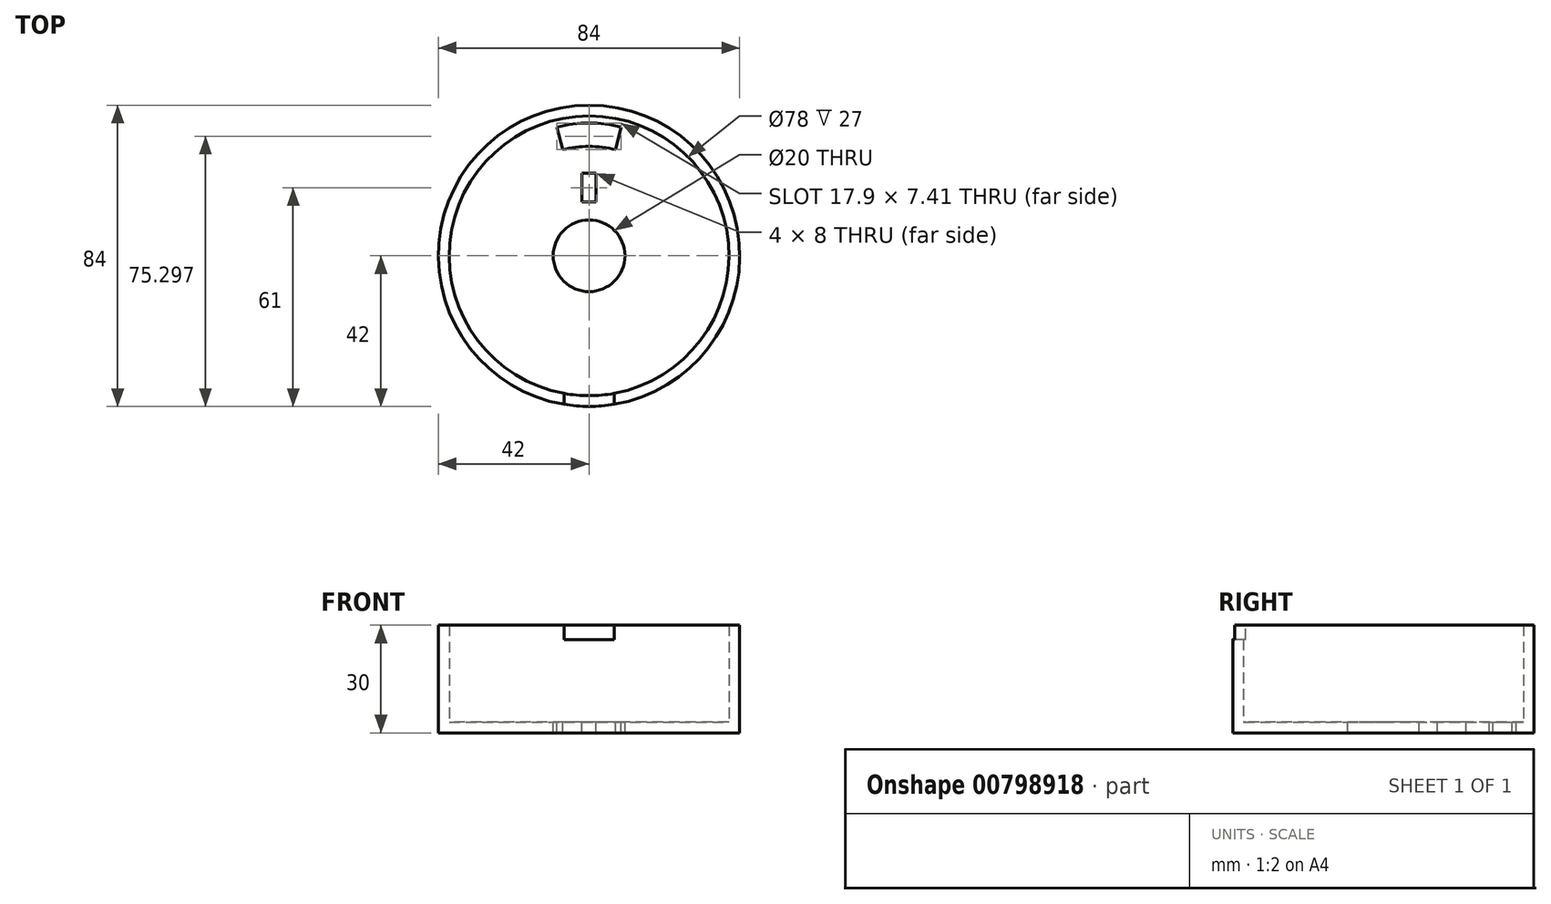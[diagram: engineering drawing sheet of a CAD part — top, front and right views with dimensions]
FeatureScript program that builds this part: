
annotation { "Feature Type Name" : "Feature", "Feature Type Description" : "" }
export const myFeature = defineFeature(function(context is Context, id is Id, definition is map)
    precondition{}
    {
        {
            var Q0;
            Q0=qCreatedBy(makeId("Top.planeOp"),FACE);
            var sketch = newSketch(context, id + "F0", { "sketchPlane" : qUnion([Q0])});
            skCircle(sketch, "E0", {"center": v(0, 0) * mm, "radius": 42 * mm});
            skSolve(sketch);
        }
        {
            var Q0;
            Q0=makeQuery(id+"F0.imprint","IMPRINT",FACE,{"disambiguationData":[TD([[makeQuery(id+"F0.imprint","IMPRINT",EDGE,{"derivedFrom":sQuery(id+"F0.wireOp",EDGE,"E0")}),1.0]])]});
            extrude(context, id + "F1", {"entities" : qUnion([Q0]), "depth" : 3 * mm, "offsetDistance" : 25.4 * mm});
        }
        {
            var Q0;
            Q0=makeQuery(id+"F1.opExtrude","CAP_FACE",FACE,{"disambiguationData":[OSD([sQuery(id+"F0.wireOp",EDGE,"E0")])],"isStart":false});
            var sketch = newSketch(context, id + "F2", { "sketchPlane" : qUnion([Q0])});
            skCircle(sketch, "E1", {"center": v(0, 0) * mm, "radius": 39 * mm});
            skCircle(sketch, "E2", {"center": v(0, 0) * mm, "radius": 42 * mm});
            skSolve(sketch);
        }
        {
            var Q0;
            Q0=makeQuery(id+"F2.imprint","IMPRINT",FACE,{"disambiguationData":[TD([[makeQuery(id+"F2.imprint","IMPRINT",EDGE,{"derivedFrom":sQuery(id+"F2.wireOp",EDGE,"E1")}),-1.0]])]});
            extrude(context, id + "F3", {"entities" : qUnion([Q0]), "operationType" : NewBodyOperationType.ADD, "depth" : 27 * mm, "offsetDistance" : 25.4 * mm});
        }
        {
            var Q0;
            Q0=makeQuery(id+"F3.opExtrude","CAP_FACE",FACE,{"disambiguationData":[OSD([sQuery(id+"F2.wireOp",EDGE,"E1"),sQuery(id+"F2.wireOp",EDGE,"E2")])],"isStart":false});
            var sketch = newSketch(context, id + "F4", { "sketchPlane" : qUnion([Q0])});
            skLineSegment(sketch, "E3.bottom", {"start": v(-7, -34.99) * mm, "end": v(7, -34.99) * mm});
            skLineSegment(sketch, "E3.top", {"start": v(-7, -46.24) * mm, "end": v(7, -46.24) * mm});
            skLineSegment(sketch, "E3.left", {"start": v(-7, -34.99) * mm, "end": v(-7, -46.24) * mm});
            skLineSegment(sketch, "E3.right", {"start": v(7, -34.99) * mm, "end": v(7, -46.24) * mm});
            skSolve(sketch);
        }
        {
            var Q0;
            {var subQ0=sQuery(id+"F4.wireOp",EDGE,"E3.left");var subQ1=makeQuery(id+"F3.opExtrude","CAP_EDGE",EDGE,{"disambiguationData":[OSD([sQuery(id+"F2.wireOp",EDGE,"E2")])],"isStart":false});var subQ2=makeQuery(id+"F4.imprint","INTERSECT",VERTEX,{"derivedFrom":[subQ1,subQ0]});Q0=makeQuery(id+"F4.imprint","IMPRINT",FACE,{"disambiguationData":[TD([[makeQuery(id+"F4.imprint","IMPRINT",EDGE,{"disambiguationData":[TD([[subQ2,1.0]])],"derivedFrom":subQ0}),1.0]])]});}
            extrude(context, id + "F5", {"entities" : qUnion([Q0]), "operationType" : NewBodyOperationType.REMOVE, "oppositeDirection" : true, "depth" : 4 * mm, "offsetDistance" : 25.4 * mm});
        }
        {
            var Q0;
            Q0=makeQuery(id+"F1.opExtrude","CAP_FACE",FACE,{"disambiguationData":[OSD([sQuery(id+"F0.wireOp",EDGE,"E0")])],"isStart":false});
            var sketch = newSketch(context, id + "F6", { "sketchPlane" : qUnion([Q0])});
            skCircle(sketch, "E4", {"center": v(0, 0) * mm, "radius": 37 * mm});
            skArc(sketch, "E5", {"start": v(7.38, 29.6) * mm, "mid": v(0, 30.5) * mm, "end": v(-7.38, 29.6) * mm});
            skLineSegment(sketch, "E6", {"start": v(7.38, 29.6) * mm, "end": v(9.43, 37.84) * mm});
            skLineSegment(sketch, "E7", {"start": v(-7.38, 29.6) * mm, "end": v(-9.43, 37.84) * mm});
            skSolve(sketch);
        }
        {
            var Q0;
            Q0=makeQuery(id+"F6.imprint","IMPRINT",FACE,{"disambiguationData":[TD([[makeQuery(id+"F6.imprint","IMPRINT",EDGE,{"derivedFrom":sQuery(id+"F6.wireOp",EDGE,"E5")}),-1.0]])]});
            extrude(context, id + "F7", {"entities" : qUnion([Q0]), "operationType" : NewBodyOperationType.REMOVE, "oppositeDirection" : true, "depth" : 25.4 * mm, "offsetDistance" : 25.4 * mm});
        }
        {
            var Q0;
            Q0=makeQuery(id+"F1.opExtrude","CAP_FACE",FACE,{"disambiguationData":[OSD([sQuery(id+"F0.wireOp",EDGE,"E0")])],"isStart":false});
            var sketch = newSketch(context, id + "F8", { "sketchPlane" : qUnion([Q0])});
            skCircle(sketch, "E8", {"center": v(0, 0) * mm, "radius": 10 * mm});
            skSolve(sketch);
        }
        {
            var Q0;
            Q0 = qSketchRegion(id + "F8", true);
            extrude(context, id + "F9", {"entities" : qUnion([Q0]), "operationType" : NewBodyOperationType.REMOVE, "oppositeDirection" : true, "depth" : 25.4 * mm, "offsetDistance" : 25.4 * mm});
        }
        {
            var Q0;
            Q0=makeQuery(id+"F1.opExtrude","CAP_FACE",FACE,{"disambiguationData":[OSD([sQuery(id+"F0.wireOp",EDGE,"E0")])],"isStart":false});
            var sketch = newSketch(context, id + "F10", { "sketchPlane" : qUnion([Q0])});
            skLineSegment(sketch, "E9.bottom", {"start": v(-2, 23) * mm, "end": v(2, 23) * mm});
            skLineSegment(sketch, "E9.top", {"start": v(-2, 15) * mm, "end": v(2, 15) * mm});
            skLineSegment(sketch, "E9.left", {"start": v(-2, 23) * mm, "end": v(-2, 15) * mm});
            skLineSegment(sketch, "E9.right", {"start": v(2, 23) * mm, "end": v(2, 15) * mm});
            skSolve(sketch);
        }
        {
            var Q0;
            Q0=makeQuery(id+"F10.imprint","IMPRINT",FACE,{"disambiguationData":[TD([[makeQuery(id+"F10.imprint","IMPRINT",EDGE,{"derivedFrom":sQuery(id+"F10.wireOp",EDGE,"E9.bottom")}),-1.0]])]});
            extrude(context, id + "F11", {"entities" : qUnion([Q0]), "operationType" : NewBodyOperationType.REMOVE, "oppositeDirection" : true, "depth" : 25.4 * mm, "offsetDistance" : 25.4 * mm});
        }
    });
